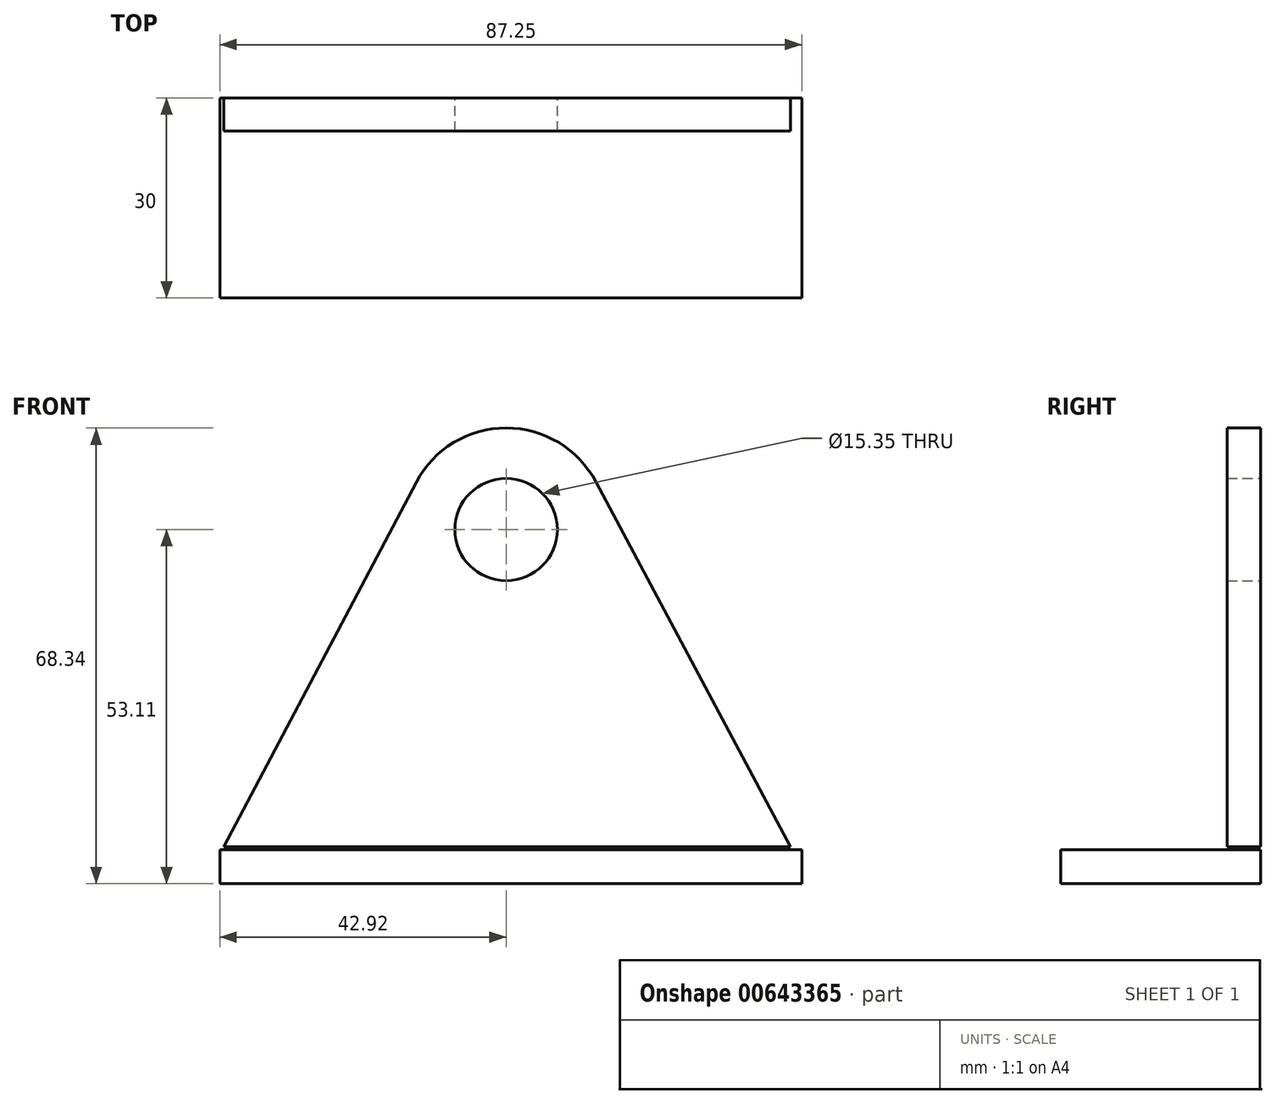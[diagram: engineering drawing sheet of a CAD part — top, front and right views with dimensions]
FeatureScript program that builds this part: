
annotation { "Feature Type Name" : "Feature", "Feature Type Description" : "" }
export const myFeature = defineFeature(function(context is Context, id is Id, definition is map)
    precondition{}
    {
        {
            var Q0;
            Q0=qCreatedBy(makeId("Front.planeOp"),FACE);
            var sketch = newSketch(context, id + "F0", { "sketchPlane" : qUnion([Q0])});
            skCircle(sketch, "E0", {"center": v(0, 0) * mm, "radius": 7.67 * mm});
            skArc(sketch, "E1", {"start": v(13.47, 7.12) * mm, "mid": v(0, 15.23) * mm, "end": v(-13.47, 7.12) * mm});
            skLineSegment(sketch, "E2", {"start": v(-42.36, -47.56) * mm, "end": v(42.64, -47.56) * mm});
            skPoint(sketch, "E3.end.orphan", {"position": v(42.64, -51.03) * mm});
            skPoint(sketch, "E4.end.orphan", {"position": v(0, -51.03) * mm});
            skPoint(sketch, "E4.start.orphan", {"position": v(-42.36, -51.03) * mm});
            skLineSegment(sketch, "E5", {"start": v(-42.36, -47.56) * mm, "end": v(-13.47, 7.12) * mm});
            skLineSegment(sketch, "E6", {"start": v(42.64, -47.56) * mm, "end": v(13.47, 7.12) * mm});
            skSolve(sketch);
        }
        {
            var Q0;
            Q0=makeQuery(id+"F0.imprint","IMPRINT",FACE,{"disambiguationData":[TD([[makeQuery(id+"F0.imprint","IMPRINT",EDGE,{"derivedFrom":sQuery(id+"F0.wireOp",EDGE,"E0")}),-1.0]])]});
            extrude(context, id + "F1", {"entities" : qUnion([Q0]), "depth" : 5 * mm, "offsetDistance" : 25 * mm});
        }
        {
            var Q0;
            Q0=qCreatedBy(makeId("Front.planeOp"),FACE);
            var sketch = newSketch(context, id + "F2", { "sketchPlane" : qUnion([Q0])});
            skLineSegment(sketch, "E7.bottom", {"start": v(-42.92, -48.01) * mm, "end": v(44.33, -48.01) * mm});
            skLineSegment(sketch, "E7.top", {"start": v(-42.92, -53.11) * mm, "end": v(44.33, -53.11) * mm});
            skLineSegment(sketch, "E7.left", {"start": v(-42.92, -48.01) * mm, "end": v(-42.92, -53.11) * mm});
            skLineSegment(sketch, "E7.right", {"start": v(44.33, -48.01) * mm, "end": v(44.33, -53.11) * mm});
            skSolve(sketch);
        }
        {
            var Q0;
            Q0=makeQuery(id+"F2.imprint","IMPRINT",FACE,{"disambiguationData":[TD([[makeQuery(id+"F2.imprint","IMPRINT",EDGE,{"derivedFrom":sQuery(id+"F2.wireOp",EDGE,"E7.bottom")}),-1.0]])]});
            extrude(context, id + "F3", {"entities" : qUnion([Q0]), "depth" : 30 * mm, "offsetDistance" : 25 * mm});
        }
    });
